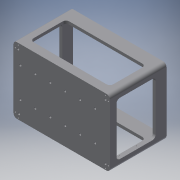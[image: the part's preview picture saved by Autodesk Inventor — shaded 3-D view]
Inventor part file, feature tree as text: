
AUTODESK INVENTOR PART (.ipt)
format: ipt  version: 2019.4 (Build 234330000, 330)  size: 384,512 bytes
history: native  units: mm
features: sketch x9, other x9, extrude x8, plane x6, reference x6, projected_geometry x5, fillet x1, hole x1
ambient origin geometry x8: Origin, YZ Plane, XZ Plane, XY Plane, X Axis, Y Axis, Z Axis, Center Point
bodies: Volumenkörper1 (feature_tree)
feature tree (45):
  plane  "Arbeitsebene1"
  extrude  "Extrusion1"  Depth=4.0mm TaperAngle=0.0deg
  sketch  "Skizze3"  dims[d16=4.1mm d17=64.1mm d18=0.0mm]
  plane  "Arbeitsebene2"
  plane  "Arbeitsebene3"
  plane  "Arbeitsebene4"
  extrude  "Extrusion2"  Depth=64.1mm TaperAngle=0.0deg
  extrude  "Extrusion3"  Depth=4.0mm
  extrude  "Extrusion4"  Depth=4.0mm
  fillet  "Rundung1"  Radius=3.0mm
  hole  "Bohrung2"  [1 undecoded]
  extrude  "Extrusion5"  Depth=105.0mm
  extrude  "Extrusion6"  Depth=10.0mm TaperAngle=0.0deg
  extrude  "Extrusion7"  Depth=10.0mm
  plane  "Work Plane5"
  plane  "Work Plane6"
  extrude  "Extrusion8"  Depth=10.0mm
  sketch  "Skizze1"  dims[d0=4.5mm d1=4.0mm d2=0.0mm]
  reference  "Referenz1"
  reference  "Referenz2"
  reference  "Referenz3"
  reference  "Referenz4"
  projected_geometry  "Projizierte Kontur1"
  sketch  "Skizze4"  dims[d20=3.0mm d21=0.0mm d22=4.0mm]
  projected_geometry  "Projizierte Kontur2"
  sketch  "Skizze5"  dims[d23=8.0mm d24=4.0mm d25=3.0mm d26=0.0mm]
  projected_geometry  "Projizierte Kontur3"
  sketch  "Skizze6"  dims[d27=4.0mm d28=112.0mm]
  sketch  "Skizze7"  dims[d29=67.0mm d30=105.0mm]
  sketch  "Skizze8"  dims[d31=76.0mm]
  reference  "Referenz7"
  projected_geometry  "Projizierte Kontur5"
  sketch  "Sketch9"  dims[d32=2.7mm d33=6.0mm d34=6.0mm d35=2.0mm d36=90.0deg d37=12.0mm d38=20.594885mm d39=10.0mm d40=0.0mm]
  projected_geometry  "Projected Loop6"
  sketch  "Sketch10"  dims[d41=1.8mm d42=1.8mm d43=2.5mm d44=2.5mm d45=10.0mm d46=0.0mm d47=2.8mm d48=2.8mm d49=2.8mm d50=2.8mm d51=4.0mm d52=0.0mm d53=80.0mm d54=71.0mm d55=108.0mm d56=4.1mm d57=71.8mm d58=108.8mm d59=54.4mm d60=71.8mm d61=35.9mm d62=10.0mm d63=0.0mm]
  reference  "Reference9"
  other  "Full_HITscope_v0.iam"
  other  "Assembly_Omniscope_v1:11"
  other  "02_Camera_Lid:1"
  other  "Assembly_Omniscope_v1:12"
  other  "Assembly_Omniscope_v1:2"
  other  "Assembly_Omniscope_v1:1"
  other  "07_Omnivision_Lamp_arm:1"
  other  "00_Microlinearmotor:1"
  other  "<userpath>\Documents\Inventor\HITscope\Full_HITscope_v0.iam"
note: 1 required parameter value undecoded (feature->parameter linkage not recoverable at this tier; creation-order binding heuristic only, values carry confidence <= 0.55)
